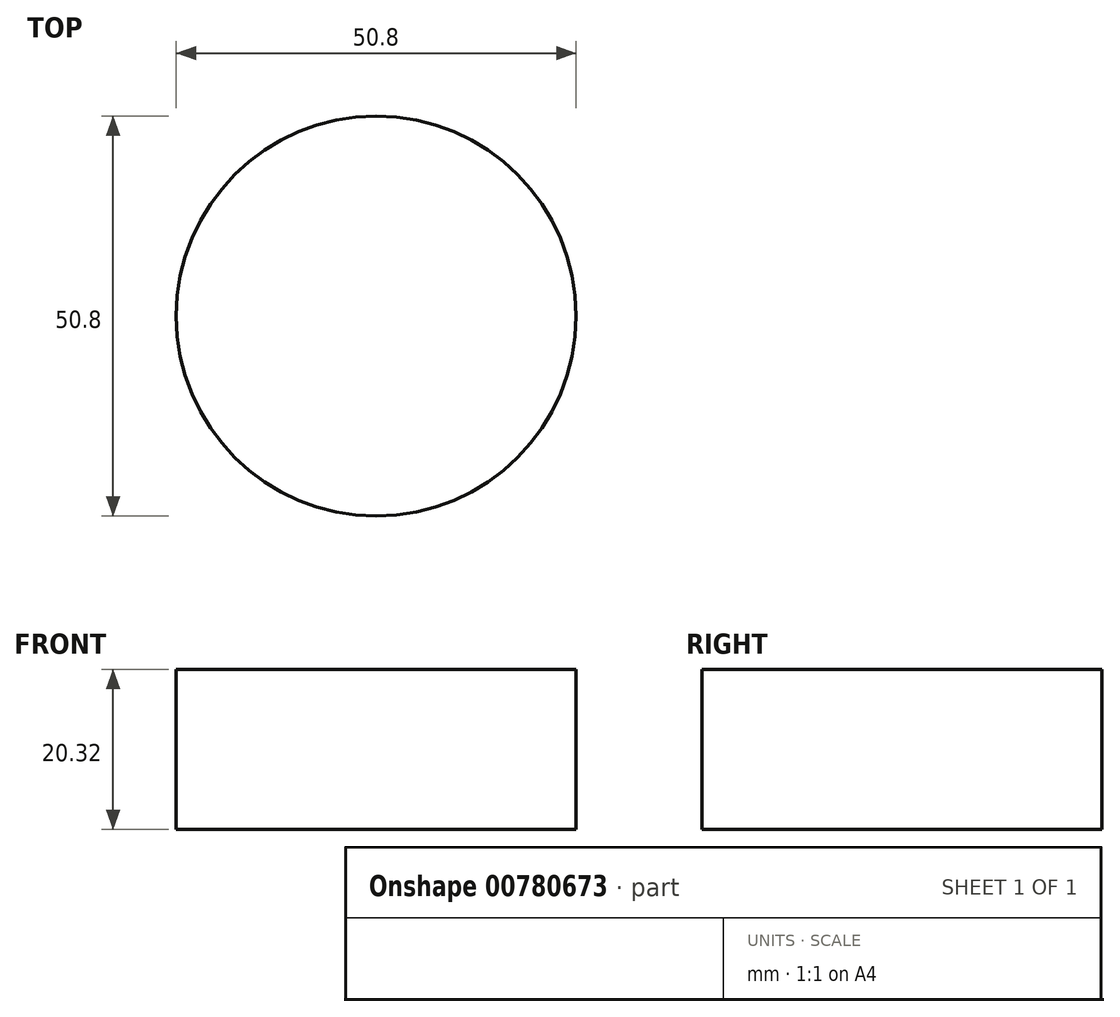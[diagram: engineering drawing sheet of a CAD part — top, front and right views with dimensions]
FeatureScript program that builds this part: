
annotation { "Feature Type Name" : "Feature", "Feature Type Description" : "" }
export const myFeature = defineFeature(function(context is Context, id is Id, definition is map)
    precondition{}
    {
        {
            var Q0;
            Q0=qCreatedBy(makeId("Top.planeOp"),FACE);
            var sketch = newSketch(context, id + "F0", { "sketchPlane" : qUnion([Q0])});
            skCircle(sketch, "E0", {"center": v(0, 0) * mm, "radius": 25.4 * mm});
            skSolve(sketch);
        }
        {
            var Q0;
            Q0=makeQuery(id+"F0.imprint","IMPRINT",FACE,{"disambiguationData":[TD([[makeQuery(id+"F0.imprint","IMPRINT",EDGE,{"derivedFrom":sQuery(id+"F0.wireOp",EDGE,"E0")}),1.0]])]});
            extrude(context, id + "F1", {"entities" : qUnion([Q0]), "depth" : 20.32 * mm, "offsetDistance" : 25.4 * mm});
        }
    });
